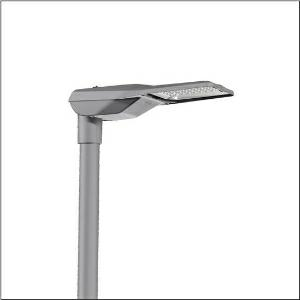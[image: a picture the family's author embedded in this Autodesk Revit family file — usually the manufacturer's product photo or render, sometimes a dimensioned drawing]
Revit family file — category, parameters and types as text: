
# Revit family: streetlight_sl_21_mini___st1_5a_5xe2p33s08hb_d0bc
name_source: partatom
category: Lighting Fixtures
units: mm (PartAtom-declared; Revit-internal decimal feet)

## family parameters
Cut with Voids When Loaded = No
Host = Face
Light Source = No
Part Type = Normal
Room Calculation Point = No
Round Connector Dimension = Use Diameter
Shared = No

## types (1)
- --- (1 x LED, 8890 lm, 66 W, 3000K)
    Apparent Load = 66 VA
    CIE Flux Codes = 22 53 95 100 100
    Color Rendering = 70
    Color Temperature = 3000K
    Default Elevation = 1800 mm
    Description = Streetlight SL 21 mini, mast luminaire, primary light control with lens, of PMMA, primary optical cover: cover, of toughened safety glass, transparent, light distribution: ST1.5a, light emission: direct distribution, primary light characteristic: asymmetric, installation type: side-entry, post-top, LED, High Power LED, rated luminous flux: 8.890lm, luminous efficacy: 135lm/W, light colour: 730, colour temperature: 3000K, control gear: D4i, control: overheat protection, constant luminous flux control, time-dependent luminous flux control, flexible luminous flux parameterisation, pre-setting: logarithmic dimming characteristic, mains connection: 220..240V, AC, 50/60Hz, start of lifetime: 66W, end of service life: 69W, reduction: 30W, luminaire housing, of diecast aluminium, powder-coated, Siteco® metallic grey (DB 702S), corrosivity category C5 mid according to DIN EN ISO 12944, please order mast flange separately, inclination adjustable: 0°, 5°, 10°, 15°, sealing non-destructively replaceable, multi-level sealing system, length: 628mm, width: 235mm, height: 110mm, mast flange for spigot size: 42mm (side-entry): 5XC10008XM4, 60/48mm (side-entry/post-top): 5XC10108XM2, 76/60mm (side-entry/post-top): 5XC10108XM1, mounting height: 4..8m, Smart Interface above, protection rating (complete): IP66, insulation class (complete): insulation class II (safety insulation), certification: CE, ENEC, ENEC+, VDE, impact resistance: IK10, permissible operating ambient temperature for outdoor applications: -40..+50°C, standard-compliant lighting for roads and squares, packaging unit: 1 piece

Light Distribution: ST1.5a
    Height = 110 mm
    Lamp = 1 x LED
    Lamp Light Flux = 8890 lm
    Lamp Power = 66 W
    Lamp count = 1
    Length = 625 mm
    Luminous efficacy = 135 lm/W
    Manufacturer = Siteco
    ModVariant = No
    Model = 5XE2P33S08HB
    Number of Poles = 1
    OnlyDefault = Yes
    Power Factor = 1
    Product Name = Streetlight SL 21 mini | ST1.5a
    Product group = mast luminaire | pylon top
    ProductGroupID = 6100
    Protection Class = Protection class II
    Protection Degree = IP 66
    RLX_Detail_Level = 1
    RLX_Emergency_Light_Flux = 0 lm
    RLX_Emergency_Type = 0
    RLX_Emergency_Type_DB = No
    RlxData = <blob elided: 29621 chars, md5=1f4d9f0f>
    Socket = socket
    Standby Power = 0 W
    System Light Flux = 8890 lm
    System Power = 66 W
    Type Comments = factory setting: luminous flux: 100 % | dim-lin: 254 | 670 mA
    Type Image = l_1003515.jpg
    URL = http://relux.com
    VarID = @adj_197113
    Voltage = 0 V
    Weight = 0.00 kg
    Width = 234 mm

## geometry (parser evidence)
native form markers: Blend x4, Sweep x11
no freeform markers — native parametric forms only
